# Revit family: C_ABR255_2DO_Cad_MULT_Prod
name_source: partatom
category: Detail Items
revit_build: Autodesk Revit 2015 (Build: 20140606_1530(x64)
units: mm (PartAtom-declared; Revit-internal decimal feet)

## types (4) — shared parameters
Density = 1.21 kg
Description = Angle brackets
EPD = https://www.strongtie.eu
ETA / DoP = https://www.strongtie.eu
Manufacturer = Simpson Strong-Tie
Model = ABR255
Model Disclaimer = Contact Simpson Strong-Tie Company  for more information
Model ID = 0010209404685498371876295931259379817221
Name = ABR255
ObjectType = ABR255
Product Material = Galvanised
Product Type = Angle brackets
Reference = ABR255
Technical datasheet = https://www.strongtie.eu
URL = www.strongtie.eu
UniClass Number = Pr_20_85_09_09
UniClass Title = Bracketed angle supports

## per-type parameters (varying)
| type | _visiblefront | _visibleleft | _visibleright | _visibletop |
| SST_ABR255_Front View | Yes | No | No | No |
| SST_ABR255_Top View | No | No | No | Yes |
| SST_ABR255_Left View | No | Yes | No | No |
| SST_ABR255_Right View | No | No | Yes | No |
